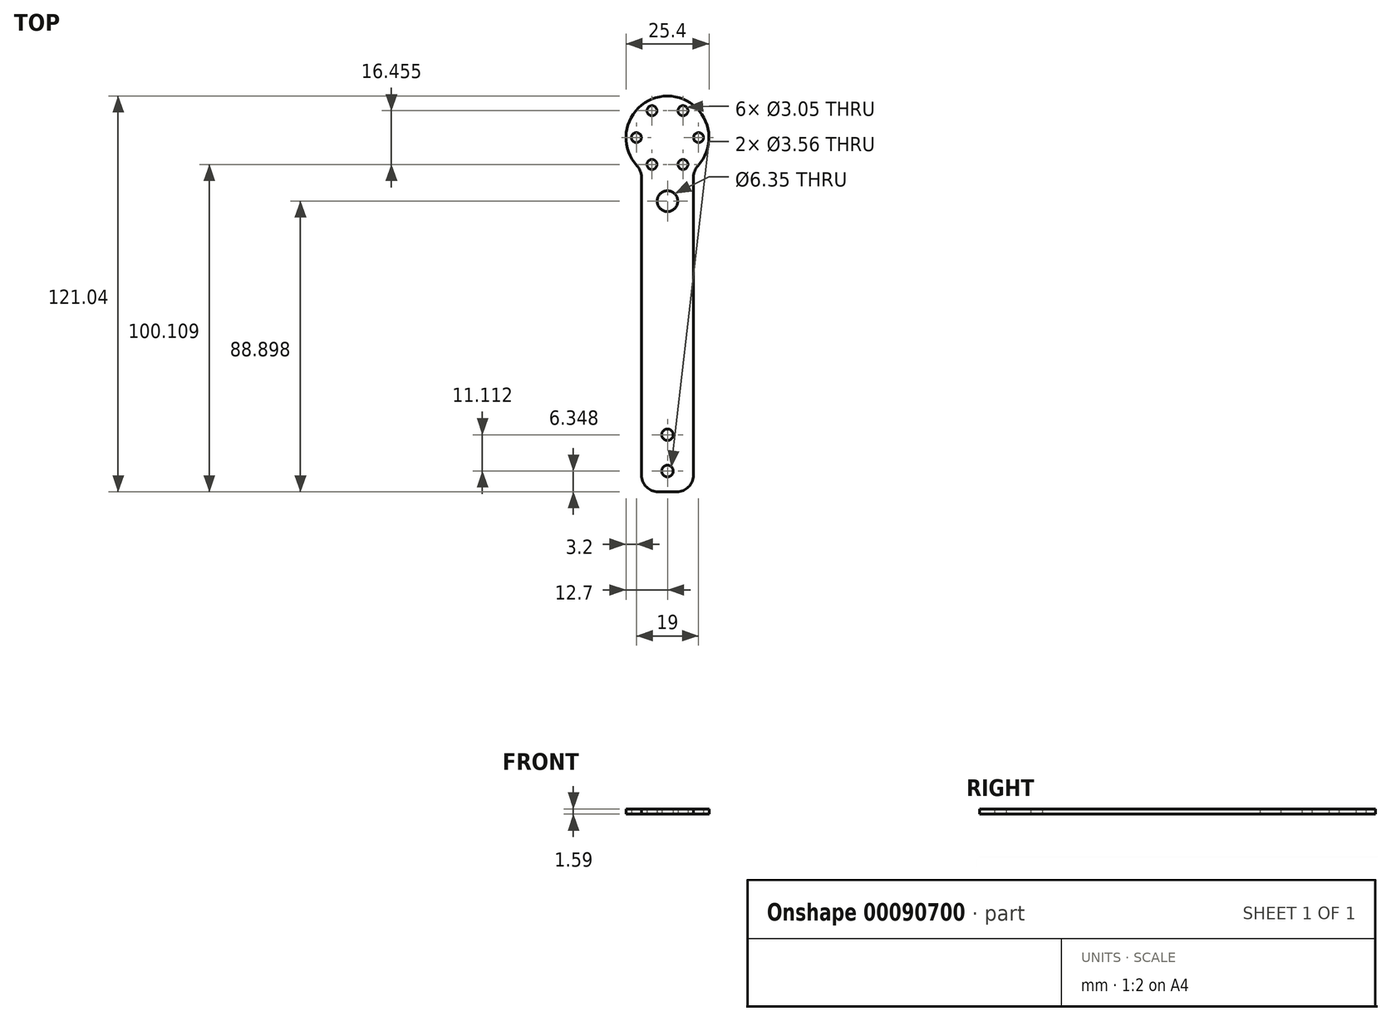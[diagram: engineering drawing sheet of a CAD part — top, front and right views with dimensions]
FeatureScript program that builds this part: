
annotation { "Feature Type Name" : "Feature", "Feature Type Description" : "" }
export const myFeature = defineFeature(function(context is Context, id is Id, definition is map)
    precondition{}
    {
        {
            var Q0;
            Q0=qCreatedBy(makeId("Top.planeOp"),FACE);
            var sketch = newSketch(context, id + "F0", { "sketchPlane" : qUnion([Q0])});
            skLineSegment(sketch, "E0.bottom", {"start": v(7.94, -49.21) * mm, "end": v(-7.94, -49.21) * mm});
            skLineSegment(sketch, "E0.left", {"start": v(7.94, -49.21) * mm, "end": v(7.94, 49.21) * mm});
            skLineSegment(sketch, "E0.right", {"start": v(-7.94, -49.21) * mm, "end": v(-7.94, 49.21) * mm});
            skPoint(sketch, "E0.middle", {"position": v(0, 0) * mm});
            skArc(sketch, "E1", {"start": v(7.94, 49.21) * mm, "mid": v(0, 71.83) * mm, "end": v(-7.94, 49.21) * mm});
            skCircle(sketch, "E2", {"center": v(0, -42.86) * mm, "radius": 1.78 * mm});
            skCircle(sketch, "E3", {"center": v(0, -31.75) * mm, "radius": 1.78 * mm});
            skCircle(sketch, "E4.cCircle", {"center": v(0, 59.13) * mm, "radius": 9.5 * mm, "construction": true});
            skLineSegment(sketch, "E4.0", {"start": v(9.5, 59.13) * mm, "end": v(4.75, 50.9) * mm, "construction": true});
            skLineSegment(sketch, "E4.1", {"start": v(4.75, 50.9) * mm, "end": v(-4.75, 50.9) * mm, "construction": true});
            skLineSegment(sketch, "E4.2", {"start": v(-4.75, 50.9) * mm, "end": v(-9.5, 59.13) * mm, "construction": true});
            skLineSegment(sketch, "E4.3", {"start": v(-9.5, 59.13) * mm, "end": v(-4.75, 67.35) * mm, "construction": true});
            skLineSegment(sketch, "E4.4", {"start": v(-4.75, 67.35) * mm, "end": v(4.75, 67.35) * mm, "construction": true});
            skLineSegment(sketch, "E4.5", {"start": v(4.75, 67.35) * mm, "end": v(9.5, 59.13) * mm, "construction": true});
            skCircle(sketch, "E5", {"center": v(9.5, 59.13) * mm, "radius": 1.52 * mm});
            skCircle(sketch, "E6", {"center": v(4.75, 50.9) * mm, "radius": 1.52 * mm});
            skCircle(sketch, "E7", {"center": v(-4.75, 50.9) * mm, "radius": 1.52 * mm});
            skCircle(sketch, "E8", {"center": v(-9.5, 59.13) * mm, "radius": 1.52 * mm});
            skCircle(sketch, "E9", {"center": v(-4.75, 67.35) * mm, "radius": 1.52 * mm});
            skCircle(sketch, "E10", {"center": v(4.75, 67.35) * mm, "radius": 1.52 * mm});
            skCircle(sketch, "E11", {"center": v(0, 39.69) * mm, "radius": 3.18 * mm});
            skSolve(sketch);
        }
        {
            var Q0;
            Q0=makeQuery(id+"F0.imprint","IMPRINT",FACE,{"disambiguationData":[TD([[makeQuery(id+"F0.imprint","IMPRINT",EDGE,{"derivedFrom":sQuery(id+"F0.wireOp",EDGE,"E0.bottom")}),-1.0]])]});
            extrude(context, id + "F1", {"entities" : qUnion([Q0]), "depth" : 1.59 * mm});
        }
        {
            var Q0;
            Q0=makeQuery(id+"F1.opExtrude","SWEPT_EDGE",EDGE,{"disambiguationData":[OSD([sQuery(id+"F0.wireOp",EDGE,"E0.left"),sQuery(id+"F0.wireOp",EDGE,"E1")])]});
            var Q1;
            Q1=makeQuery(id+"F1.opExtrude","SWEPT_EDGE",EDGE,{"disambiguationData":[OSD([sQuery(id+"F0.wireOp",EDGE,"E0.bottom"),sQuery(id+"F0.wireOp",EDGE,"E0.left")])]});
            var Q2;
            Q2=makeQuery(id+"F1.opExtrude","SWEPT_EDGE",EDGE,{"disambiguationData":[OSD([sQuery(id+"F0.wireOp",EDGE,"E0.bottom"),sQuery(id+"F0.wireOp",EDGE,"E0.right")])]});
            var Q3;
            Q3=makeQuery(id+"F1.opExtrude","SWEPT_EDGE",EDGE,{"disambiguationData":[OSD([sQuery(id+"F0.wireOp",EDGE,"E0.right"),sQuery(id+"F0.wireOp",EDGE,"E1")])]});
            fillet(context, id + "F2", {"entities" : qUnion([Q0, Q1, Q2, Q3]), "radius" : 5.08 * mm, "tangentPropagation" : true, "allowEdgeOverflow" : false});
        }
    });
